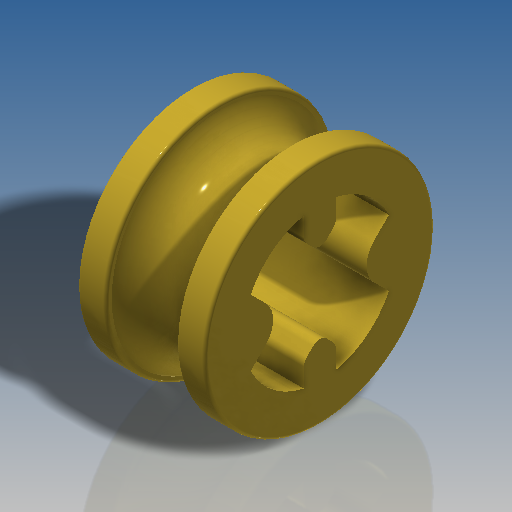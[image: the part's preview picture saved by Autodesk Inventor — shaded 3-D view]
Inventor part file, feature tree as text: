
AUTODESK INVENTOR PART (.ipt)
format: ipt  version: 2019.4 (Build 234330000, 330)  size: 330,752 bytes
history: native  units: mm
features: fillet x2, sketch x2, revolve x1, extrude x1
ambient origin geometry x8: Origin, YZ Plane, XZ Plane, XY Plane, X Axis, Y Axis, Z Axis, Center Point
bodies: Solid1 (feature_tree)
feature tree (6):
  revolve  "Revolution1"  [1 undecoded]
  extrude  "Extrusion1"  Depth=1.2mm
  fillet  "Fillet1"  Radius=4.0mm
  fillet  "Fillet2"  Radius=4.0mm
  sketch  "Sketch1"  dims[d0=0.1mm d1=7.2mm]
  sketch  "Sketch2"  dims[d2=5.4mm d3=5.4mm d4=4.0mm d5=4.0mm d10=90.0deg d11=4.8mm d12=1.6mm d13=1.0mm d14=1.0mm d15=1.462742mm d16=1.462742mm d17=1.6mm d18=1.6mm d19=1.6mm d20=10.0mm d21=0.0mm d22=0.3mm d23=0.8mm d24=0.0mm d25=0.0mm d26=2.2mm d27=1.2mm d28=0.0mm]
note: 1 required parameter value undecoded (feature->parameter linkage not recoverable at this tier; creation-order binding heuristic only, values carry confidence <= 0.55)
